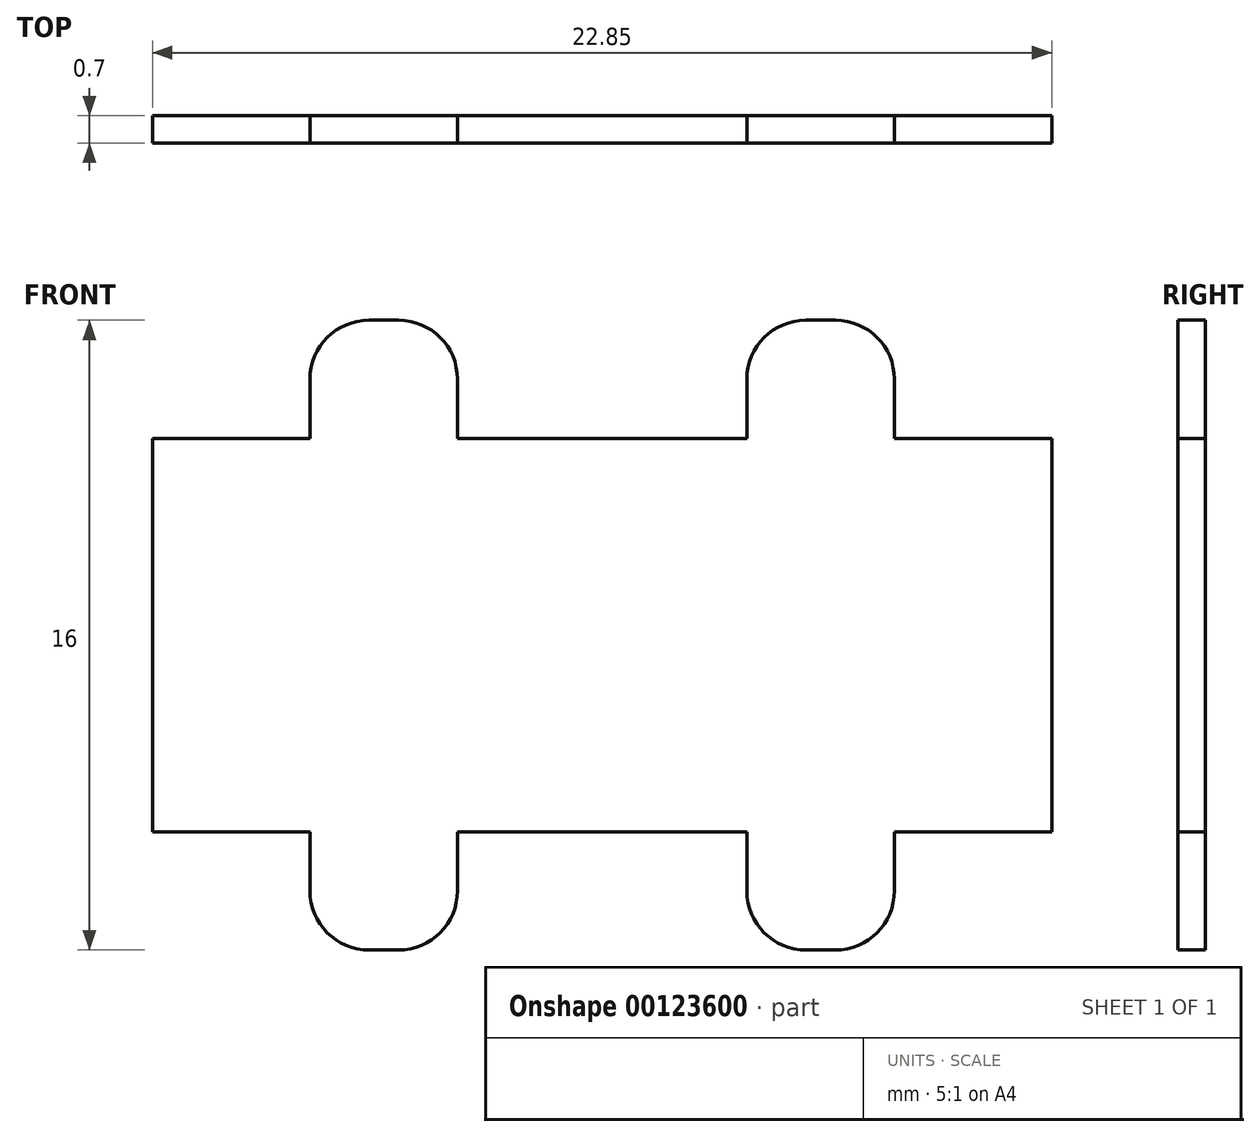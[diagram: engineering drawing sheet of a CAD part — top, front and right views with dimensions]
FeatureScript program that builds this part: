
annotation { "Feature Type Name" : "Feature", "Feature Type Description" : "" }
export const myFeature = defineFeature(function(context is Context, id is Id, definition is map)
    precondition{}
    {
        {
            var Q0;
            Q0=qCreatedBy(makeId("Front.planeOp"),FACE);
            var sketch = newSketch(context, id + "F0", { "sketchPlane" : qUnion([Q0])});
            skLineSegment(sketch, "E0.bottom", {"start": v(3.75, 0) * mm, "end": v(11.1, 0) * mm});
            skLineSegment(sketch, "E0.top", {"start": v(3.75, 10) * mm, "end": v(11.1, 10) * mm});
            skLineSegment(sketch, "E1", {"start": v(0, 10) * mm, "end": v(0, 13) * mm});
            skLineSegment(sketch, "E2", {"start": v(0, 13) * mm, "end": v(3.75, 13) * mm});
            skLineSegment(sketch, "E3", {"start": v(3.75, 13) * mm, "end": v(3.75, 10) * mm});
            skLineSegment(sketch, "E4", {"start": v(-4, 5) * mm, "end": v(18.85, 5) * mm, "construction": true});
            skLineSegment(sketch, "E5", {"start": v(7.42, 10) * mm, "end": v(7.42, 0) * mm, "construction": true});
            skLineSegment(sketch, "E6.MirrorCS", {"start": v(14.85, 13) * mm, "end": v(11.1, 13) * mm});
            skLineSegment(sketch, "E7.MirrorCS", {"start": v(14.85, 10) * mm, "end": v(14.85, 13) * mm});
            skLineSegment(sketch, "E8.MirrorCS", {"start": v(11.1, 13) * mm, "end": v(11.1, 10) * mm});
            skLineSegment(sketch, "E9.MirrorCS", {"start": v(0, 0) * mm, "end": v(0, -3) * mm});
            skLineSegment(sketch, "E10.MirrorCS", {"start": v(0, -3) * mm, "end": v(3.75, -3) * mm});
            skLineSegment(sketch, "E11.MirrorCS", {"start": v(3.75, -3) * mm, "end": v(3.75, 0) * mm});
            skLineSegment(sketch, "E12.MirrorCS", {"start": v(11.1, -3) * mm, "end": v(11.1, 0) * mm});
            skLineSegment(sketch, "E13.MirrorCS", {"start": v(14.85, -3) * mm, "end": v(11.1, -3) * mm});
            skLineSegment(sketch, "E14.MirrorCS", {"start": v(14.85, 0) * mm, "end": v(14.85, -3) * mm});
            skLineSegment(sketch, "E15", {"start": v(0, 10) * mm, "end": v(-4, 10) * mm});
            skLineSegment(sketch, "E16.MirrorCS", {"start": v(14.85, 10) * mm, "end": v(18.85, 10) * mm});
            skLineSegment(sketch, "E17.MirrorCS", {"start": v(0, 0) * mm, "end": v(-4, 0) * mm});
            skLineSegment(sketch, "E18.MirrorCS", {"start": v(14.85, 0) * mm, "end": v(18.85, 0) * mm});
            skLineSegment(sketch, "E19", {"start": v(-4, 10) * mm, "end": v(-4, 0) * mm});
            skLineSegment(sketch, "E20", {"start": v(18.85, 0) * mm, "end": v(18.85, 10) * mm});
            skPoint(sketch, "E0.left.start.orphan", {"position": v(0, 0) * mm});
            skPoint(sketch, "E21.orphan", {"position": v(14.85, 10) * mm});
            skPoint(sketch, "E0.right.start.orphan", {"position": v(14.85, 0) * mm});
            skPoint(sketch, "E22.orphan", {"position": v(0, 5) * mm});
            skPoint(sketch, "E23.orphan", {"position": v(14.85, 5) * mm});
            skSolve(sketch);
        }
        {
            var Q0;
            Q0=makeQuery(id+"F0.imprint","IMPRINT",FACE,{"disambiguationData":[TD([[makeQuery(id+"F0.imprint","IMPRINT",EDGE,{"derivedFrom":sQuery(id+"F0.wireOp",EDGE,"E0.bottom")}),1.0]])]});
            extrude(context, id + "F1", {"entities" : qUnion([Q0]), "depth" : .7 * mm});
        }
        {
            var Q0;
            Q0=makeQuery(id+"F1.opExtrude","SWEPT_EDGE",EDGE,{"disambiguationData":[OSD([sQuery(id+"F0.wireOp",EDGE,"E1"),sQuery(id+"F0.wireOp",EDGE,"E2")])]});
            var Q1;
            Q1=makeQuery(id+"F1.opExtrude","SWEPT_EDGE",EDGE,{"disambiguationData":[OSD([sQuery(id+"F0.wireOp",EDGE,"E2"),sQuery(id+"F0.wireOp",EDGE,"E3")])]});
            var Q2;
            Q2=makeQuery(id+"F1.opExtrude","SWEPT_EDGE",EDGE,{"disambiguationData":[OSD([sQuery(id+"F0.wireOp",EDGE,"E6.MirrorCS"),sQuery(id+"F0.wireOp",EDGE,"E8.MirrorCS")])]});
            var Q3;
            Q3=makeQuery(id+"F1.opExtrude","SWEPT_EDGE",EDGE,{"disambiguationData":[OSD([sQuery(id+"F0.wireOp",EDGE,"E6.MirrorCS"),sQuery(id+"F0.wireOp",EDGE,"E7.MirrorCS")])]});
            var Q4;
            Q4=makeQuery(id+"F1.opExtrude","SWEPT_EDGE",EDGE,{"disambiguationData":[OSD([sQuery(id+"F0.wireOp",EDGE,"E9.MirrorCS"),sQuery(id+"F0.wireOp",EDGE,"E10.MirrorCS")])]});
            var Q5;
            Q5=makeQuery(id+"F1.opExtrude","SWEPT_EDGE",EDGE,{"disambiguationData":[OSD([sQuery(id+"F0.wireOp",EDGE,"E10.MirrorCS"),sQuery(id+"F0.wireOp",EDGE,"E11.MirrorCS")])]});
            var Q6;
            Q6=makeQuery(id+"F1.opExtrude","SWEPT_EDGE",EDGE,{"disambiguationData":[OSD([sQuery(id+"F0.wireOp",EDGE,"E12.MirrorCS"),sQuery(id+"F0.wireOp",EDGE,"E13.MirrorCS")])]});
            var Q7;
            Q7=makeQuery(id+"F1.opExtrude","SWEPT_EDGE",EDGE,{"disambiguationData":[OSD([sQuery(id+"F0.wireOp",EDGE,"E13.MirrorCS"),sQuery(id+"F0.wireOp",EDGE,"E14.MirrorCS")])]});
            fillet(context, id + "F2", {"entities" : qUnion([Q0, Q1, Q2, Q3, Q4, Q5, Q6, Q7]), "radius" : 1.5 * mm, "tangentPropagation" : true, "allowEdgeOverflow" : false});
        }
    });
